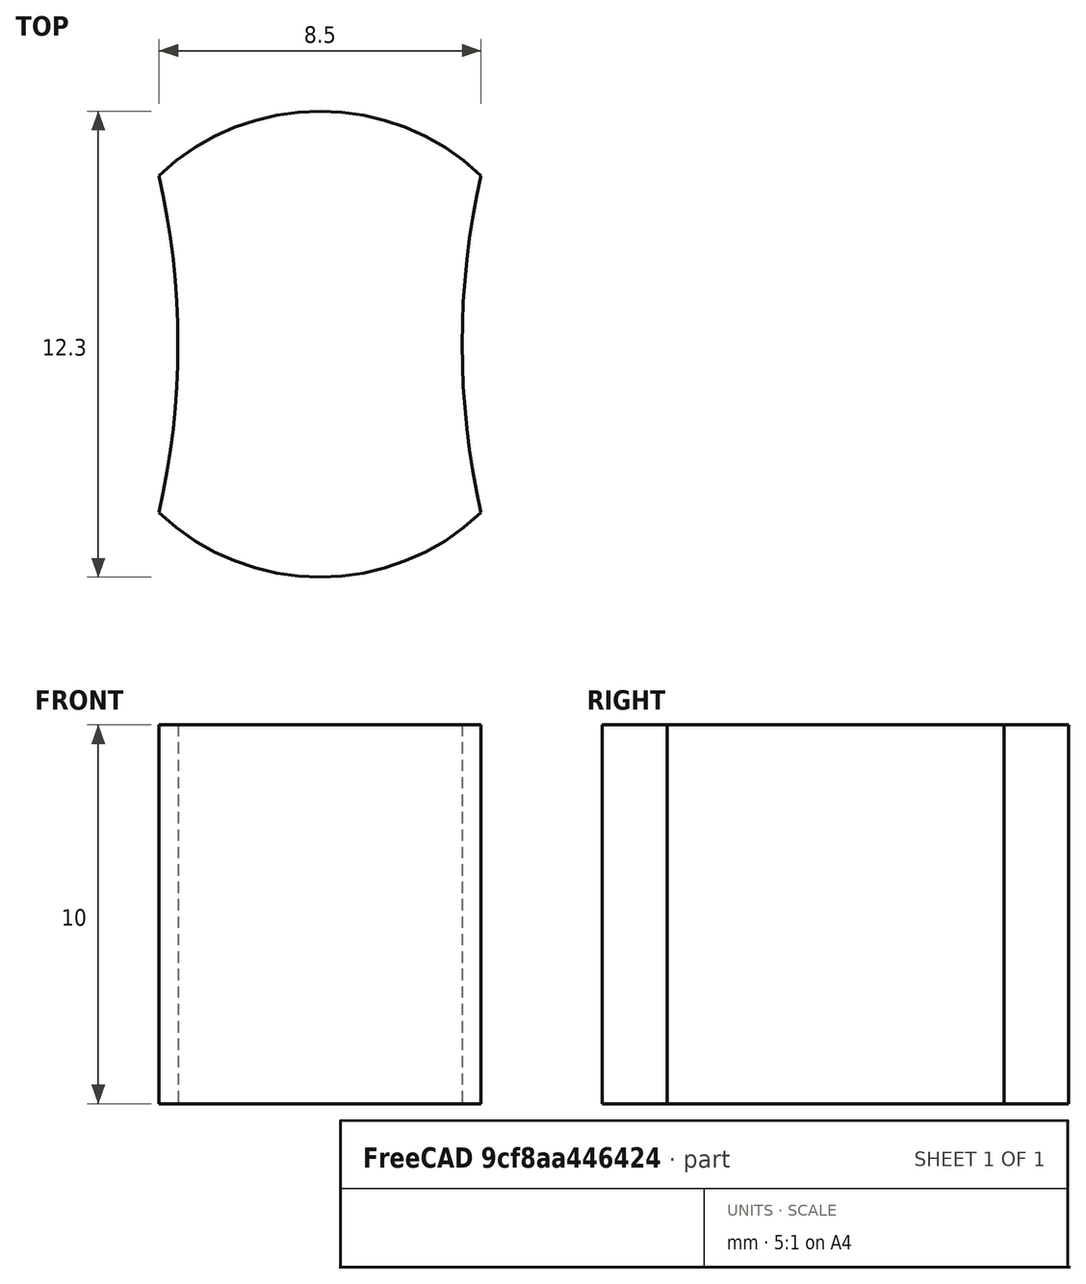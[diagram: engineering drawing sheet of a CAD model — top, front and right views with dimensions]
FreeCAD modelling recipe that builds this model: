
FCSTD DOCUMENT  (FreeCAD 0.17R13541 (Git))
Label: test122_bikefix
License: All rights reserved
LicenseURL: http://en.wikipedia.org/wiki/All_rights_reserved
objects: Sketcher::SketchObject×1, PartDesign::Pad×1, PartDesign::Body×1
note: 4 computed .brp shape members not serialized (recipe doc carries the construction recipe); baked Part::Feature solids carry a one-line shape summary decoded from their .brp

FEATURE [Sketcher::SketchObject] Sketch
  MapMode = 5
  Support = -> [XY_Plane]
  sketch-geometry (13):
    g0: LineSegment [constr] StartX=0 StartY=0 StartZ=0 EndX=7.5 EndY=0 EndZ=0
    g1: LineSegment [constr] StartX=7.5 StartY=0 StartZ=0 EndX=7.5 EndY=40 EndZ=0
    g2: LineSegment [constr] StartX=7.5 StartY=40 StartZ=0 EndX=0 EndY=40 EndZ=0
    g3: LineSegment [constr] StartX=0 StartY=40 StartZ=0 EndX=0 EndY=0 EndZ=0
    g4: Circle [constr] CenterX=27.5 CenterY=20 CenterZ=0 NormalX=0 NormalY=0 NormalZ=1 AngleXU=0 Radius=20
    g5: ArcOfCircle CenterX=27.5 CenterY=20 CenterZ=0 NormalX=0 NormalY=0 NormalZ=1 AngleXU=0 Radius=20 StartAngle=2.91752 EndAngle=3.36567
    g6: Circle [constr] CenterX=-20 CenterY=20 CenterZ=0 NormalX=0 NormalY=0 NormalZ=1 AngleXU=0 Radius=20
    g7: ArcOfCircle CenterX=-20 CenterY=20 CenterZ=0 NormalX=0 NormalY=0 NormalZ=1 AngleXU=0 Radius=20 StartAngle=6.05911 EndAngle=6.50726
    g8: LineSegment [constr] StartX=-0.5 StartY=24.4441 StartZ=0 EndX=8 EndY=24.4441 EndZ=0
    g9: LineSegment [constr] StartX=8 StartY=15.5559 StartZ=0 EndX=-0.5 EndY=15.5559 EndZ=0
    g10: ArcOfCircle CenterX=3.75 CenterY=20 CenterZ=0 NormalX=0 NormalY=0 NormalZ=1 AngleXU=0 Radius=6.14919 StartAngle=3.94931 EndAngle=5.47547
    g11: LineSegment [constr] StartX=-0.5 StartY=15.5559 StartZ=0 EndX=8 EndY=24.4441 EndZ=0
    g12: ArcOfCircle CenterX=3.75 CenterY=20 CenterZ=0 NormalX=0 NormalY=0 NormalZ=1 AngleXU=0 Radius=6.14919 StartAngle=0.80772 EndAngle=2.33387
  constraints (39):
    c: Coincident(g0,g1)
    c: Coincident(g1,g2)
    c: Coincident(g2,g3)
    c: Coincident(g3,g0)
    c: Horizontal(g0)
    c: Horizontal(g2)
    c: Vertical(g1)
    c: Vertical(g3)
    c: Coincident(g0,g-1)
    c: Distance(g2) = 7.5
    c: Distance(g1) = 40
    c: Radius(g4) = 20
    c: Tangent(g4,g1)
    c: Tangent(g4,g-1)
    c: PointOnObject(g5,g4)
    c: PointOnObject(g5,g4)
    c: Distance(g5,g1) = 0.5
    c: Coincident(g5,g4)
    c: Equal(g4,g6) = 20
    c: Tangent(g6,g3)
    c: Tangent(g-1,g6)
    c: PointOnObject(g7,g6)
    c: PointOnObject(g7,g6)
    c: Coincident(g7,g6)
    c: Coincident(g8,g7)
    c: Coincident(g8,g5)
    c: Coincident(g9,g5)
    c: Coincident(g9,g7)
    c: Equal(g9,g8)
    c: Coincident(g10,g7)
    c: Coincident(g10,g5)
    c: Horizontal(g9)
    c: Horizontal(g8)
    c: Coincident(g11,g7)
    c: Coincident(g11,g5)
    c: PointOnObject(g10,g11)
    c: Coincident(g12,g10)
    c: Coincident(g12,g7)
    c: Coincident(g12,g5)
FEATURE [PartDesign::Pad] Pad
  Length = 10
  Length2 = 100
  Profile = -> Sketch
  Type = 0
FEATURE [PartDesign::Body] Body
  Group = -> [Sketch,Pad]
  Origin = -> Origin
  Tip = -> Pad
